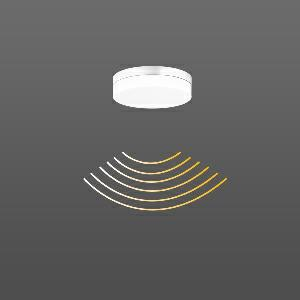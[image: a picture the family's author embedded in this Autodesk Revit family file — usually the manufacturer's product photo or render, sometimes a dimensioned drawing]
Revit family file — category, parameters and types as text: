
# Revit family: flat_slim_round_312135_002_2_19_949f
name_source: partatom
category: Lighting Fixtures
units: mm (PartAtom-declared; Revit-internal decimal feet)

## family parameters
Cut with Voids When Loaded = No
Host = Face
Light Source = No
Part Type = Normal
Room Calculation Point = No
Round Connector Dimension = Use Diameter
Shared = No

## types (1)
- FLAT SLIM round (1 x LED Modul 830, 1300 lm, 3000)
    Apparent Load = 12 VA
    CIE Flux Codes = 43 74 92 91 100
    Color Rendering = 80
    Color Temperature = 3000
    Default Elevation = 1800 mm
    Height = 63 mm
    Lamp = 1 x LED Modul 830
    Lamp Light Flux = 1300 lm
    Lamp count = 1
    Length = 230 mm
    Lifetime = 50000 h
    Luminous efficacy = 108 lm/W
    Manufacturer = RZB
    ModVariant = No
    Model = 312135.002.2.19
    Mounting Place = Ceiling, Wall
    Mounting Type = Surface mounted
    Number of Poles = 1
    OnlyDefault = Yes
    Power Factor = 1
    Product Name = FLAT SLIM round
    Product group = Surface mounted ceiling and wall luminaires
    ProductGroupID = 305
    Protection Class = Protection class I
    Protection Degree = IP 65
    RLX_Detail_Level = 1
    RLX_Emergency_Light_Flux = 0 lm
    RLX_Emergency_Type = 0
    RLX_Emergency_Type_DB = No
    RlxData = <blob elided: 32061 chars, md5=d5d8e455>
    Socket = socket
    Standby Power = 0 W
    System Light Flux = 1300 lm
    System Power = 12 W
    Type Comments = Product without accessories
    Type Image = 312132.002.19.jpg
    URL = http://relux.com
    VarID = ---
    Voltage = 230 V
    Voltage Range = 220-240 V
    Weight = 0.00 kg
    Width = 0 mm  [stored 0 ft]

note: [stored X ft] marks values corroborated as IEEE doubles in the binary element streams (Revit-internal decimal feet)

## geometry (parser evidence)
native form markers: Blend x4, Sweep x14
no freeform markers — native parametric forms only
